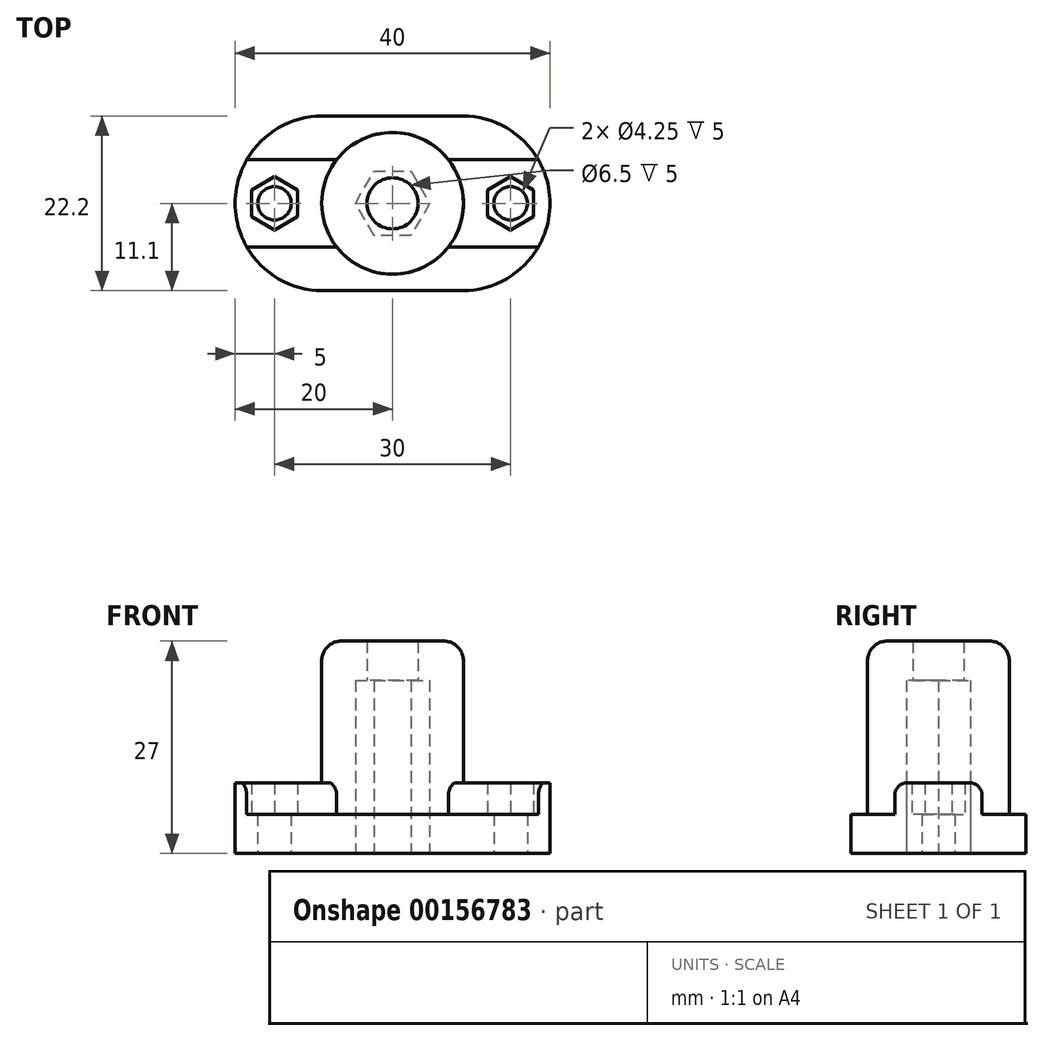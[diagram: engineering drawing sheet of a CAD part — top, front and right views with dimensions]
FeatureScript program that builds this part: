
annotation { "Feature Type Name" : "Feature", "Feature Type Description" : "" }
export const myFeature = defineFeature(function(context is Context, id is Id, definition is map)
    precondition{}
    {
        {
            var Q0;
            Q0=qCreatedBy(makeId("Top.planeOp"),FACE);
            var sketch = newSketch(context, id + "F0", { "sketchPlane" : qUnion([Q0])});
            skCircle(sketch, "E0.cCircle", {"center": v(0, 0) * mm, "radius": 4.1 * mm, "construction": true});
            skLineSegment(sketch, "E0.0", {"start": v(-2.36, 4.1) * mm, "end": v(2.36, 4.1) * mm});
            skLineSegment(sketch, "E0.1", {"start": v(2.36, 4.1) * mm, "end": v(4.72, 0) * mm});
            skLineSegment(sketch, "E0.2", {"start": v(4.72, 0) * mm, "end": v(2.36, -4.1) * mm});
            skLineSegment(sketch, "E0.3", {"start": v(2.36, -4.09) * mm, "end": v(-2.36, -4.1) * mm});
            skLineSegment(sketch, "E0.4", {"start": v(-2.36, -4.1) * mm, "end": v(-4.72, 0) * mm});
            skLineSegment(sketch, "E0.5", {"start": v(-4.72, 0) * mm, "end": v(-2.36, 4.1) * mm});
            skPoint(sketch, "E0.0.midPoint", {"position": v(0, 4.1) * mm});
            skLineSegment(sketch, "E1.bottom", {"start": v(20, -11.1) * mm, "end": v(-20, -11.1) * mm});
            skLineSegment(sketch, "E1.top", {"start": v(20, 11.1) * mm, "end": v(-20, 11.1) * mm});
            skLineSegment(sketch, "E1.left", {"start": v(20, -11.1) * mm, "end": v(20, 11.1) * mm});
            skLineSegment(sketch, "E1.right", {"start": v(-20, -11.1) * mm, "end": v(-20, 11.1) * mm});
            skCircle(sketch, "E2", {"center": v(-15, 0) * mm, "radius": 2.12 * mm});
            skCircle(sketch, "E3.MirrorC", {"center": v(15, 0) * mm, "radius": 2.12 * mm});
            skSolve(sketch);
        }
        {
            var Q0;
            Q0=qSketchRegion(id+"F0",true);
            extrude(context, id + "F1", {"entities" : qUnion([Q0]), "depth" : 5 * mm});
        }
        {
            var Q0;
            Q0=makeQuery(id+"F1.opExtrude","CAP_FACE",FACE,{"disambiguationData":[OSD([sQuery(id+"F0.wireOp",EDGE,"E0.0"),sQuery(id+"F0.wireOp",EDGE,"E0.1"),sQuery(id+"F0.wireOp",EDGE,"E0.2"),sQuery(id+"F0.wireOp",EDGE,"E0.3"),sQuery(id+"F0.wireOp",EDGE,"E0.4"),sQuery(id+"F0.wireOp",EDGE,"E0.5"),sQuery(id+"F0.wireOp",EDGE,"E1.bottom"),sQuery(id+"F0.wireOp",EDGE,"E1.top"),sQuery(id+"F0.wireOp",EDGE,"E1.left"),sQuery(id+"F0.wireOp",EDGE,"E1.right"),sQuery(id+"F0.wireOp",EDGE,"E2"),sQuery(id+"F0.wireOp",EDGE,"E3.MirrorC")])],"isStart":false});
            var sketch = newSketch(context, id + "F2", { "sketchPlane" : qUnion([Q0])});
            skCircle(sketch, "E4", {"center": v(0, 0) * mm, "radius": 9 * mm});
            skCircle(sketch, "E5.cCircle", {"center": v(0, 0) * mm, "radius": 4.1 * mm, "construction": true});
            skLineSegment(sketch, "E5.0", {"start": v(-2.36, 4.1) * mm, "end": v(2.36, 4.1) * mm});
            skLineSegment(sketch, "E5.1", {"start": v(2.36, 4.1) * mm, "end": v(4.72, 0) * mm});
            skLineSegment(sketch, "E5.2", {"start": v(4.72, 0) * mm, "end": v(2.36, -4.1) * mm});
            skLineSegment(sketch, "E5.3", {"start": v(2.36, -4.09) * mm, "end": v(-2.36, -4.1) * mm});
            skLineSegment(sketch, "E5.4", {"start": v(-2.36, -4.1) * mm, "end": v(-4.72, 0) * mm});
            skLineSegment(sketch, "E5.5", {"start": v(-4.72, 0) * mm, "end": v(-2.36, 4.1) * mm});
            skPoint(sketch, "E5.0.midPoint", {"position": v(0, 4.1) * mm});
            skSolve(sketch);
        }
        {
            var Q0;
            Q0=qSketchRegion(id+"F2",true);
            extrude(context, id + "F3", {"entities" : qUnion([Q0]), "operationType" : NewBodyOperationType.ADD, "depth" : 17 * mm});
        }
        {
            var Q0;
            Q0=makeQuery(id+"F3.opExtrude","CAP_FACE",FACE,{"disambiguationData":[OSD([sQuery(id+"F2.wireOp",EDGE,"E4"),sQuery(id+"F2.wireOp",EDGE,"E5.0"),sQuery(id+"F2.wireOp",EDGE,"E5.1"),sQuery(id+"F2.wireOp",EDGE,"E5.2"),sQuery(id+"F2.wireOp",EDGE,"E5.3"),sQuery(id+"F2.wireOp",EDGE,"E5.4"),sQuery(id+"F2.wireOp",EDGE,"E5.5")])],"isStart":false});
            var sketch = newSketch(context, id + "F4", { "sketchPlane" : qUnion([Q0])});
            skCircle(sketch, "E6", {"center": v(0, 0) * mm, "radius": 3.25 * mm});
            skCircle(sketch, "E7", {"center": v(0, 0) * mm, "radius": 9 * mm});
            skSolve(sketch);
        }
        {
            var Q0;
            Q0=qSketchRegion(id+"F4",true);
            extrude(context, id + "F5", {"entities" : qUnion([Q0]), "operationType" : NewBodyOperationType.ADD, "depth" : 5 * mm});
        }
        {
            var Q0;
            Q0=makeQuery(id+"F1.opExtrude","SWEPT_EDGE",EDGE,{"disambiguationData":[OSD([sQuery(id+"F0.wireOp",EDGE,"E1.top"),sQuery(id+"F0.wireOp",EDGE,"E1.right")])]});
            var Q1;
            Q1=makeQuery(id+"F1.opExtrude","SWEPT_EDGE",EDGE,{"disambiguationData":[OSD([sQuery(id+"F0.wireOp",EDGE,"E1.bottom"),sQuery(id+"F0.wireOp",EDGE,"E1.right")])]});
            var Q2;
            Q2=makeQuery(id+"F1.opExtrude","SWEPT_EDGE",EDGE,{"disambiguationData":[OSD([sQuery(id+"F0.wireOp",EDGE,"E1.top"),sQuery(id+"F0.wireOp",EDGE,"E1.left")])]});
            var Q3;
            Q3=makeQuery(id+"F1.opExtrude","SWEPT_EDGE",EDGE,{"disambiguationData":[OSD([sQuery(id+"F0.wireOp",EDGE,"E1.bottom"),sQuery(id+"F0.wireOp",EDGE,"E1.left")])]});
            fillet(context, id + "F6", {"entities" : qUnion([Q0, Q1, Q2, Q3]), "radius" : 11.1 * mm, "tangentPropagation" : true, "allowEdgeOverflow" : false});
        }
        {
            var Q0;
            Q0=makeQuery(id+"F5.opExtrude","CAP_EDGE",EDGE,{"disambiguationData":[OSD([sQuery(id+"F4.wireOp",EDGE,"E7")])],"isStart":false});
            var Q1;
            Q1=makeQuery(id+"F3.opExtrude","CAP_EDGE",EDGE,{"disambiguationData":[OSD([sQuery(id+"F2.wireOp",EDGE,"E4")])],"isStart":true});
            fillet(context, id + "F7", {"entities" : qUnion([Q0, Q1]), "radius" : 2.5 * mm, "tangentPropagation" : true, "allowEdgeOverflow" : false});
        }
        {
            var Q0;
            Q0=makeQuery(id+"F7.opFillet","SPLIT",FACE,{"disambiguationData":[OD(1.0)],"derivedFrom":makeQuery(id+"F1.opExtrude","CAP_FACE",FACE,{"disambiguationData":[OSD([sQuery(id+"F0.wireOp",EDGE,"E0.0"),sQuery(id+"F0.wireOp",EDGE,"E0.1"),sQuery(id+"F0.wireOp",EDGE,"E0.2"),sQuery(id+"F0.wireOp",EDGE,"E0.3"),sQuery(id+"F0.wireOp",EDGE,"E0.4"),sQuery(id+"F0.wireOp",EDGE,"E0.5"),sQuery(id+"F0.wireOp",EDGE,"E1.bottom"),sQuery(id+"F0.wireOp",EDGE,"E1.top"),sQuery(id+"F0.wireOp",EDGE,"E1.left"),sQuery(id+"F0.wireOp",EDGE,"E1.right"),sQuery(id+"F0.wireOp",EDGE,"E2"),sQuery(id+"F0.wireOp",EDGE,"E3.MirrorC")])],"isStart":false})});
            var sketch = newSketch(context, id + "F8", { "sketchPlane" : qUnion([Q0])});
            skCircle(sketch, "E8.cCircle", {"center": v(15, 0) * mm, "radius": 2.93 * mm, "construction": true});
            skLineSegment(sketch, "E8.0", {"start": v(17.92, 1.69) * mm, "end": v(17.92, -1.69) * mm});
            skLineSegment(sketch, "E8.1", {"start": v(17.92, -1.69) * mm, "end": v(15, -3.38) * mm});
            skLineSegment(sketch, "E8.2", {"start": v(15, -3.38) * mm, "end": v(12.08, -1.69) * mm});
            skLineSegment(sketch, "E8.3", {"start": v(12.08, -1.69) * mm, "end": v(12.07, 1.69) * mm});
            skLineSegment(sketch, "E8.4", {"start": v(12.07, 1.69) * mm, "end": v(15, 3.38) * mm});
            skLineSegment(sketch, "E8.5", {"start": v(15, 3.38) * mm, "end": v(17.92, 1.69) * mm});
            skPoint(sketch, "E8.0.midPoint", {"position": v(17.92, 0) * mm});
            skLineSegment(sketch, "E9.bottom", {"start": v(18.51, -5.55) * mm, "end": v(6.7, -5.55) * mm});
            skLineSegment(sketch, "E9.top", {"start": v(18.51, 5.55) * mm, "end": v(6.3, 5.55) * mm});
            skLineSegment(sketch, "E9.right", {"start": v(6.7, -5.55) * mm, "end": v(6.3, 5.55) * mm});
            skArc(sketch, "E10", {"start": v(18.51, 5.55) * mm, "mid": v(20, 0) * mm, "end": v(18.51, -5.55) * mm});
            skPoint(sketch, "E9.left.end.orphan", {"position": v(23.3, 5.55) * mm});
            skPoint(sketch, "E9.left.start.orphan", {"position": v(23.7, -5.55) * mm});
            skLineSegment(sketch, "E11.MirrorCS", {"start": v(-17.92, 1.69) * mm, "end": v(-17.92, -1.69) * mm});
            skLineSegment(sketch, "E12.MirrorCS", {"start": v(-17.92, -1.69) * mm, "end": v(-15, -3.38) * mm});
            skLineSegment(sketch, "E13.MirrorCS", {"start": v(-15, -3.38) * mm, "end": v(-12.08, -1.69) * mm});
            skLineSegment(sketch, "E14.MirrorCS", {"start": v(-12.08, -1.69) * mm, "end": v(-12.07, 1.69) * mm});
            skLineSegment(sketch, "E15.MirrorCS", {"start": v(-15, 3.38) * mm, "end": v(-17.92, 1.69) * mm});
            skPoint(sketch, "E16.MirrorP", {"position": v(-23.3, 5.55) * mm});
            skCircle(sketch, "E17.MirrorC", {"center": v(-15, 0) * mm, "radius": 2.93 * mm, "construction": true});
            skLineSegment(sketch, "E18.MirrorCS", {"start": v(-12.07, 1.69) * mm, "end": v(-15, 3.38) * mm});
            skLineSegment(sketch, "E19.MirrorCS", {"start": v(-18.51, -5.55) * mm, "end": v(-6.7, -5.55) * mm});
            skLineSegment(sketch, "E20.MirrorCS", {"start": v(-18.51, 5.55) * mm, "end": v(-6.3, 5.55) * mm});
            skArc(sketch, "E21.MirrorCS", {"start": v(-18.51, 5.55) * mm, "mid": v(-20, 0) * mm, "end": v(-18.51, -5.55) * mm});
            skLineSegment(sketch, "E22.MirrorCS", {"start": v(-6.7, -5.55) * mm, "end": v(-6.3, 5.55) * mm});
            skPoint(sketch, "E23.MirrorP", {"position": v(-23.7, -5.55) * mm});
            skPoint(sketch, "E24.MirrorP", {"position": v(-17.92, 0) * mm});
            skSolve(sketch);
        }
        {
            var Q0;
            Q0 = qSketchRegion(id + "F8", true);
            extrude(context, id + "F9", {"entities" : qUnion([Q0]), "operationType" : NewBodyOperationType.ADD, "depth" : 4 * mm});
        }
        {
            var Q0;
            Q0=makeQuery(id+"F9.opExtrude","CAP_EDGE",EDGE,{"disambiguationData":[OSD([sQuery(id+"F8.wireOp",EDGE,"E20.MirrorCS")])],"isStart":false});
            var Q1;
            Q1=makeQuery(id+"F9.opExtrude","CAP_EDGE",EDGE,{"disambiguationData":[OSD([sQuery(id+"F8.wireOp",EDGE,"E19.MirrorCS")])],"isStart":false});
            var Q2;
            Q2=makeQuery(id+"F9.opExtrude","CAP_EDGE",EDGE,{"disambiguationData":[OSD([sQuery(id+"F8.wireOp",EDGE,"E9.bottom")])],"isStart":false});
            var Q3;
            Q3=makeQuery(id+"F9.opExtrude","CAP_EDGE",EDGE,{"disambiguationData":[OSD([sQuery(id+"F8.wireOp",EDGE,"E9.top")])],"isStart":false});
            fillet(context, id + "F10", {"entities" : qUnion([Q0, Q1, Q2, Q3]), "radius" : 1.6 * mm, "tangentPropagation" : true, "allowEdgeOverflow" : false});
        }
    });
